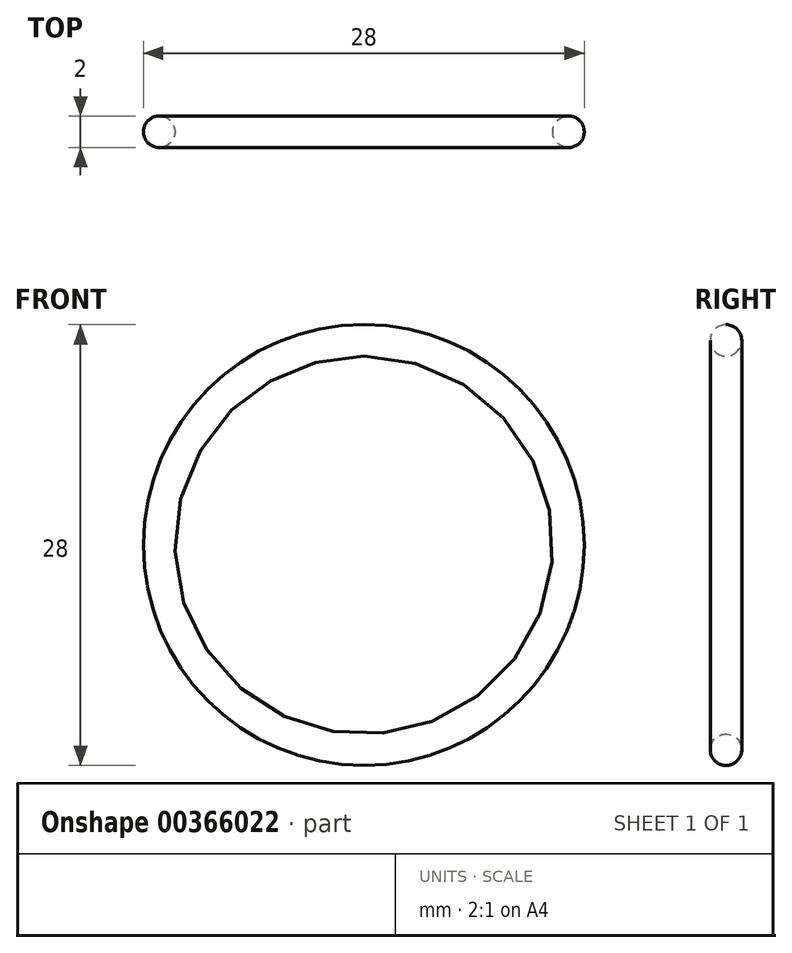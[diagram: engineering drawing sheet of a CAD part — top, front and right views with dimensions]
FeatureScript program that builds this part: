
annotation { "Feature Type Name" : "Feature", "Feature Type Description" : "" }
export const myFeature = defineFeature(function(context is Context, id is Id, definition is map)
    precondition{}
    {
        {
            var Q0;
            Q0=qCreatedBy(makeId("Top.planeOp"),FACE);
            var sketch = newSketch(context, id + "F0", { "sketchPlane" : qUnion([Q0])});
            skCircle(sketch, "E0", {"center": v(13, 0) * mm, "radius": 1 * mm});
            skSolve(sketch);
        }
        {
            var Q0;
            Q0=qCreatedBy(makeId("Top.planeOp"),FACE);
            var sketch = newSketch(context, id + "F1", { "sketchPlane" : qUnion([Q0])});
            skLineSegment(sketch, "E1", {"start": v(0, 32) * mm, "end": v(0, -27.48) * mm});
            skSolve(sketch);
        }
        {
            var Q0;
            Q0=makeQuery(id+"F0.imprint","IMPRINT",FACE,{"disambiguationData":[TD([[makeQuery(id+"F0.imprint","IMPRINT",EDGE,{"derivedFrom":sQuery(id+"F0.wireOp",EDGE,"E0")}),1.0]])]});
            var Q1;
            Q1=sQuery(id+"F1.wireOp",EDGE,"E1");
            revolve(context, id + "F2", {"entities" : qUnion([Q0]), "axis" : qUnion([Q1]), "revolveType" : RevolveType.FULL});
        }
    });
